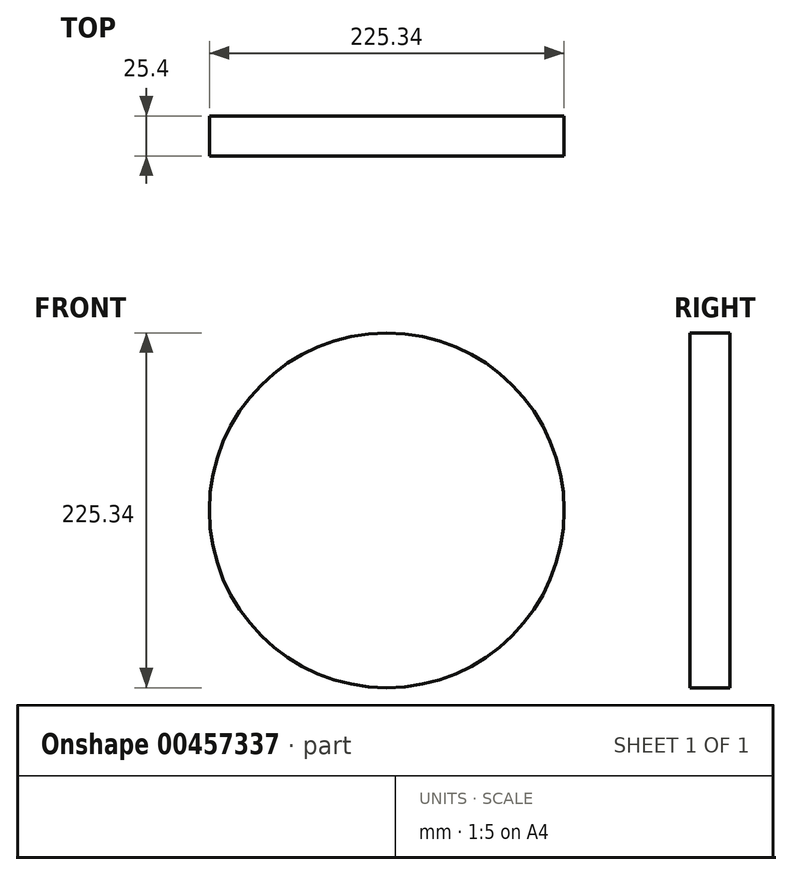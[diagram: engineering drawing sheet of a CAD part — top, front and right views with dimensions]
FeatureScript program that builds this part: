
annotation { "Feature Type Name" : "Feature", "Feature Type Description" : "" }
export const myFeature = defineFeature(function(context is Context, id is Id, definition is map)
    precondition{}
    {
        {
            var Q0;
            Q0=qCreatedBy(makeId("Front.planeOp"),FACE);
            var sketch = newSketch(context, id + "F0", { "sketchPlane" : qUnion([Q0])});
            skCircle(sketch, "E0", {"center": v(0, 0) * mm, "radius": 16.15 * mm});
            skCircle(sketch, "E1.0", {"center": v(0, 0) * mm, "radius": 112.67 * mm});
            skSolve(sketch);
        }
        {
            var Q0;
            Q0=sQuery(id+"F0.wireOp",EDGE,"E1.0");
            extrude(context, id + "F1", {"bodyType" : ToolBodyType.SURFACE, "surfaceEntities" : qUnion([Q0]), "depth" : 25.4 * mm});
        }
    });
